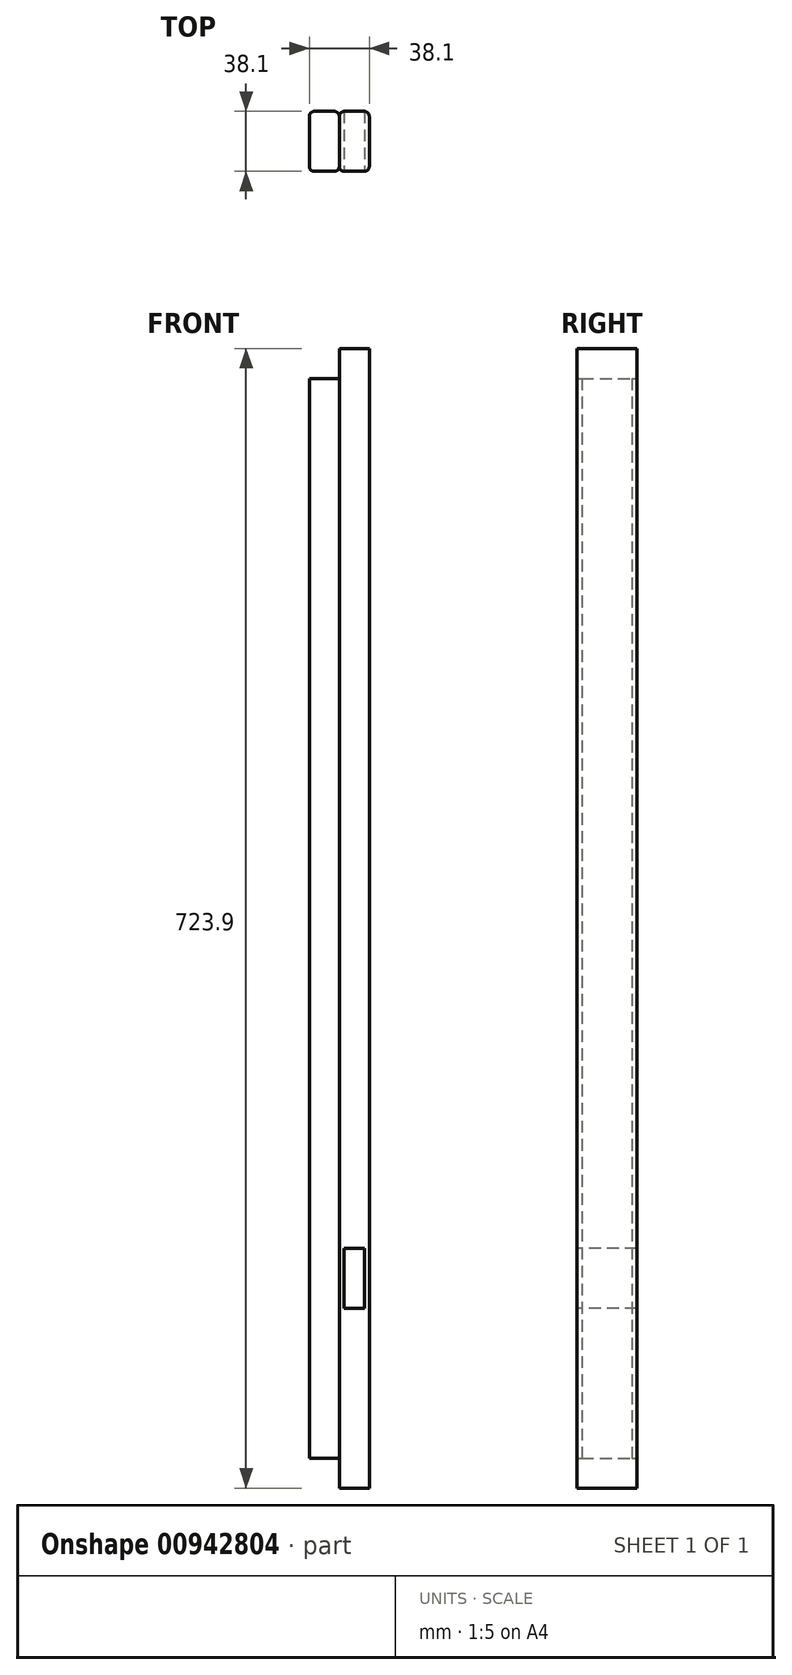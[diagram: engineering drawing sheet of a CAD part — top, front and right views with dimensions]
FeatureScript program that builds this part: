
annotation { "Feature Type Name" : "Feature", "Feature Type Description" : "" }
export const myFeature = defineFeature(function(context is Context, id is Id, definition is map)
    precondition{}
    {
        {
            var Q0;
            Q0=qCreatedBy(makeId("Top.planeOp"),FACE);
            var sketch = newSketch(context, id + "F0", { "sketchPlane" : qUnion([Q0])});
            skLineSegment(sketch, "E0.bottom", {"start": v(3.15, 0) * mm, "end": v(15.9, 0) * mm});
            skLineSegment(sketch, "E0.top", {"start": v(3.15, 38.1) * mm, "end": v(15.9, 38.1) * mm});
            skLineSegment(sketch, "E0.left", {"start": v(0, 3.15) * mm, "end": v(0, 34.95) * mm});
            skLineSegment(sketch, "E0.right", {"start": v(19.05, 3.15) * mm, "end": v(19.05, 34.95) * mm});
            skPoint(sketch, "E1.visualSharp", {"position": v(0, 38.1) * mm});
            skArc(sketch, "E1.filletArc", {"start": v(3.15, 38.1) * mm, "mid": v(0.92, 37.18) * mm, "end": v(0, 34.95) * mm});
            skArc(sketch, "E2.filletArc", {"start": v(19.05, 34.95) * mm, "mid": v(18.13, 37.18) * mm, "end": v(15.9, 38.1) * mm});
            skPoint(sketch, "E3.visualSharp", {"position": v(19.05, 0) * mm});
            skArc(sketch, "E3.filletArc", {"start": v(15.9, 0) * mm, "mid": v(18.13, 0.92) * mm, "end": v(19.05, 3.15) * mm});
            skPoint(sketch, "E4.visualSharp", {"position": v(0, 0) * mm});
            skArc(sketch, "E4.filletArc", {"start": v(0, 3.15) * mm, "mid": v(0.92, 0.92) * mm, "end": v(3.15, 0) * mm});
            skLineSegment(sketch, "E5.bottom", {"start": v(22.2, 0) * mm, "end": v(34.95, 0) * mm});
            skLineSegment(sketch, "E5.right", {"start": v(38.1, 3.15) * mm, "end": v(38.1, 34.95) * mm});
            skArc(sketch, "E6.filletArc", {"start": v(22.2, 38.1) * mm, "mid": v(19.97, 37.18) * mm, "end": v(19.05, 34.95) * mm});
            skArc(sketch, "E7.filletArc", {"start": v(38.1, 34.95) * mm, "mid": v(37.18, 37.18) * mm, "end": v(34.95, 38.1) * mm});
            skArc(sketch, "E8.filletArc", {"start": v(34.95, 0) * mm, "mid": v(37.18, 0.92) * mm, "end": v(38.1, 3.15) * mm});
            skArc(sketch, "E9.filletArc", {"start": v(19.05, 3.15) * mm, "mid": v(19.97, 0.92) * mm, "end": v(22.2, 0) * mm});
            skLineSegment(sketch, "E10", {"start": v(22.2, 38.1) * mm, "end": v(34.95, 38.1) * mm});
            skSolve(sketch);
        }
        {
            var Q0;
            Q0=makeQuery(id+"F0.imprint","IMPRINT",FACE,{"disambiguationData":[TD([[makeQuery(id+"F0.imprint","IMPRINT",EDGE,{"derivedFrom":sQuery(id+"F0.wireOp",EDGE,"E5.bottom")}),1.0]])]});
            var Q1;
            Q1=makeQuery(id+"F0.imprint","IMPRINT",FACE,{"disambiguationData":[TD([[makeQuery(id+"F0.imprint","IMPRINT",EDGE,{"derivedFrom":sQuery(id+"F0.wireOp",EDGE,"b7ff1907-7b2b-4cdd-8ea5-b45dade5522d.bottom")}),1.0]])]});
            var Q2;
            Q2=makeQuery(id+"F0.imprint","IMPRINT",FACE,{"disambiguationData":[TD([[makeQuery(id+"F0.imprint","IMPRINT",EDGE,{"derivedFrom":sQuery(id+"F0.wireOp",EDGE,"66c86851-db75-4c71-9093-7621e61d7ab7.bottom")}),1.0]])]});
            extrude(context, id + "F1", {"entities" : qUnion([Q0, Q1, Q2]), "depth" : 723.9 * mm, "offsetDistance" : 25.4 * mm});
        }
        {
            var Q0;
            Q0 = qSketchRegion(id + "F0", true);
            extrude(context, id + "F2", {"entities" : qUnion([Q0]), "operationType" : NewBodyOperationType.ADD, "depth" : 704.85 * mm, "offsetDistance" : 25.4 * mm});
        }
        {
            var Q0;
            Q0=makeQuery(id+"F0.imprint","IMPRINT",FACE,{"disambiguationData":[TD([[makeQuery(id+"F0.imprint","IMPRINT",EDGE,{"derivedFrom":sQuery(id+"F0.wireOp",EDGE,"E0.bottom")}),1.0]])]});
            extrude(context, id + "F3", {"entities" : qUnion([Q0]), "operationType" : NewBodyOperationType.REMOVE, "depth" : 19.05 * mm, "offsetDistance" : 25.4 * mm});
        }
        {
            var Q0;
            Q0=makeQuery(id+"F1.opExtrude","SWEPT_FACE",FACE,{"disambiguationData":[OSD([sQuery(id+"F0.wireOp",EDGE,"E5.bottom")])]});
            var sketch = newSketch(context, id + "F4", { "sketchPlane" : qUnion([Q0])});
            skLineSegment(sketch, "E11.0", {"start": v(38.1, 723.9) * mm, "end": v(38.1, 0) * mm});
            skLineSegment(sketch, "E12.0", {"start": v(22.2, 723.9) * mm, "end": v(34.95, 723.9) * mm});
            skLineSegment(sketch, "E13.0", {"start": v(19.05, 723.9) * mm, "end": v(22.2, 723.9) * mm});
            skLineSegment(sketch, "E14.0", {"start": v(34.95, 723.9) * mm, "end": v(38.1, 723.9) * mm});
            skLineSegment(sketch, "E15.0", {"start": v(19.05, 723.9) * mm, "end": v(19.05, 704.85) * mm});
            skLineSegment(sketch, "E16.0", {"start": v(19.05, 704.85) * mm, "end": v(19.05, 19.05) * mm});
            skLineSegment(sketch, "E17.bottom", {"start": v(38.1, 152.4) * mm, "end": v(19.05, 152.4) * mm});
            skLineSegment(sketch, "E17.top", {"start": v(38.1, 114.3) * mm, "end": v(19.05, 114.3) * mm});
            skLineSegment(sketch, "E17.left", {"start": v(38.1, 152.4) * mm, "end": v(38.1, 114.3) * mm});
            skLineSegment(sketch, "E17.right", {"start": v(19.05, 152.4) * mm, "end": v(19.05, 114.3) * mm});
            skSolve(sketch);
        }
        {
            var Q0;
            {var subQ0=sQuery(id+"F4.wireOp",EDGE,"E17.left");Q0=makeQuery(id+"F4.imprint","IMPRINT",FACE,{"disambiguationData":[TD([[makeQuery(id+"F4.imprint","IMPRINT",EDGE,{"derivedFrom":subQ0}),-1.0]])]});}
            var Q1;
            {var subQ0=sQuery(id+"F4.wireOp",EDGE,"E17.bottom");var subQ1=sQuery(id+"F0.wireOp",EDGE,"E5.bottom");var subQ2=makeQuery(id+"F1.opExtrude","SWEPT_EDGE",EDGE,{"disambiguationData":[OSD([subQ1,sQuery(id+"F0.wireOp",EDGE,"E8.filletArc")])]});var subQ3=makeQuery(id+"F4.imprint","INTERSECT",VERTEX,{"derivedFrom":[subQ2,subQ0]});Q1=makeQuery(id+"F4.imprint","IMPRINT",FACE,{"disambiguationData":[TD([[makeQuery(id+"F4.imprint","IMPRINT",EDGE,{"disambiguationData":[TD([[subQ3,-1.0]])],"derivedFrom":subQ0}),1.0]])]});}
            var Q2;
            {var subQ0=sQuery(id+"F4.wireOp",EDGE,"E17.right");Q2=makeQuery(id+"F4.imprint","IMPRINT",FACE,{"disambiguationData":[TD([[makeQuery(id+"F4.imprint","IMPRINT",EDGE,{"derivedFrom":subQ0}),1.0]])]});}
            extrude(context, id + "F5", {"entities" : qUnion([Q0, Q1, Q2]), "operationType" : NewBodyOperationType.REMOVE, "endBound" : BoundingType.THROUGH_ALL, "oppositeDirection" : true, "depth" : 25.4 * mm, "offsetDistance" : 25.4 * mm});
        }
    });
